# Revit family: Sanitary_Accessories_DURAVIT_D-Code-Towel-rail-009924_
name_source: partatom
category: Furniture
revit_build: Autodesk Revit 2015 (Build: 20140903_1530(x64)
units: mm (PartAtom-declared; Revit-internal decimal feet)

## types (1)
- Default
    BIMobject category = Accessories
    BIMobject category code = sanitary-accessories1
    BIMobject main category = Sanitary
    BIMobject main category code = sanitary
    Brand url = http://www.duravit.com
    Edition number = 1
    GTIN code = 4021534636219
    IFC Classification = Sanitary Terminal
    Installation instructions = http://pro.duravit.com
    Manufacturer name = DURAVIT
    Masterformat 2014 Code = 10 28 00
    Masterformat 2014 Description = Toilet, Bath, and Laundry Accessories
    Material main = Chrome
    NBS Reference Code = 35-75-90
    NBS Reference Description = Towel Rails
    OmniClass Code = 23-31 25 25
    OmniClass Description = Towel Bars
    Product Guid = 9dfe2030-6437-4a28-adf9-1fe8478d93d7
    Product SKU = d-code-towel-rail-009924
    Product certification = http://pro.duravit.com
    Product data url = https://bimobject.com
    Product family = D-Code
    Product group = wash area accessories
    Product name = D-Code Towel rail 009924
    Product url = http://pro.duravit.com
    QR code = http://bimobject.com
    Technical description = http://pro.duravit.com
    UNSPSC Code = 301815
    Uniclass 1.4 Code = L8245
    Uniclass 1.4 Description = Towel rails
    Uniclass 2.0 Code = PR-35-75-90
    Uniclass 2.0 Description = Towel Rails
    Uniclass 2015 Code = Pr_40_20_76_90
    Uniclass 2015 Name = Towel rails
    Uniformat II Code = E2010
    Uniformat II Description = Fixed Furnishings
    Youtube clip = http://pro.duravit.com

## geometry (parser evidence)
native form markers: Sweep x3
no freeform markers — native parametric forms only
